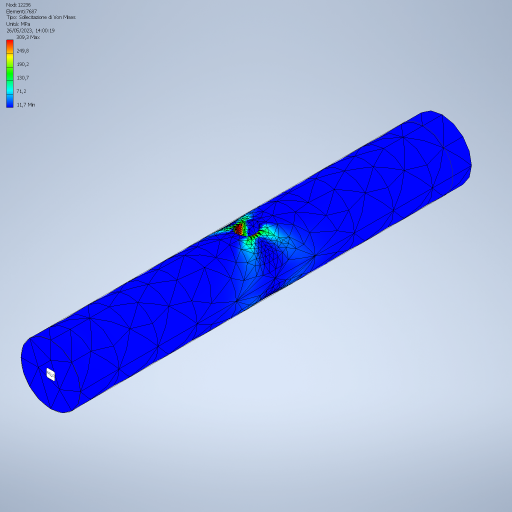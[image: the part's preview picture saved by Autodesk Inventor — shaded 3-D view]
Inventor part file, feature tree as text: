
AUTODESK INVENTOR PART (.ipt)
format: ipt  version: 2023 (Build 270158000, 158)  size: 317,952 bytes
history: native  units: mm
features: extrude x2, sketch x2
ambient origin geometry x8: Origin, YZ Plane, XZ Plane, XY Plane, X Axis, Y Axis, Z Axis, Center Point
bodies: Solido1 (feature_tree)
feature tree (4):
  extrude  "Estrusione1"  Depth=40.0mm
  extrude  "Estrusione2"  Depth=250.0mm TaperAngle=0.0deg
  sketch  "Schizzo1"
  sketch  "Schizzo2"
